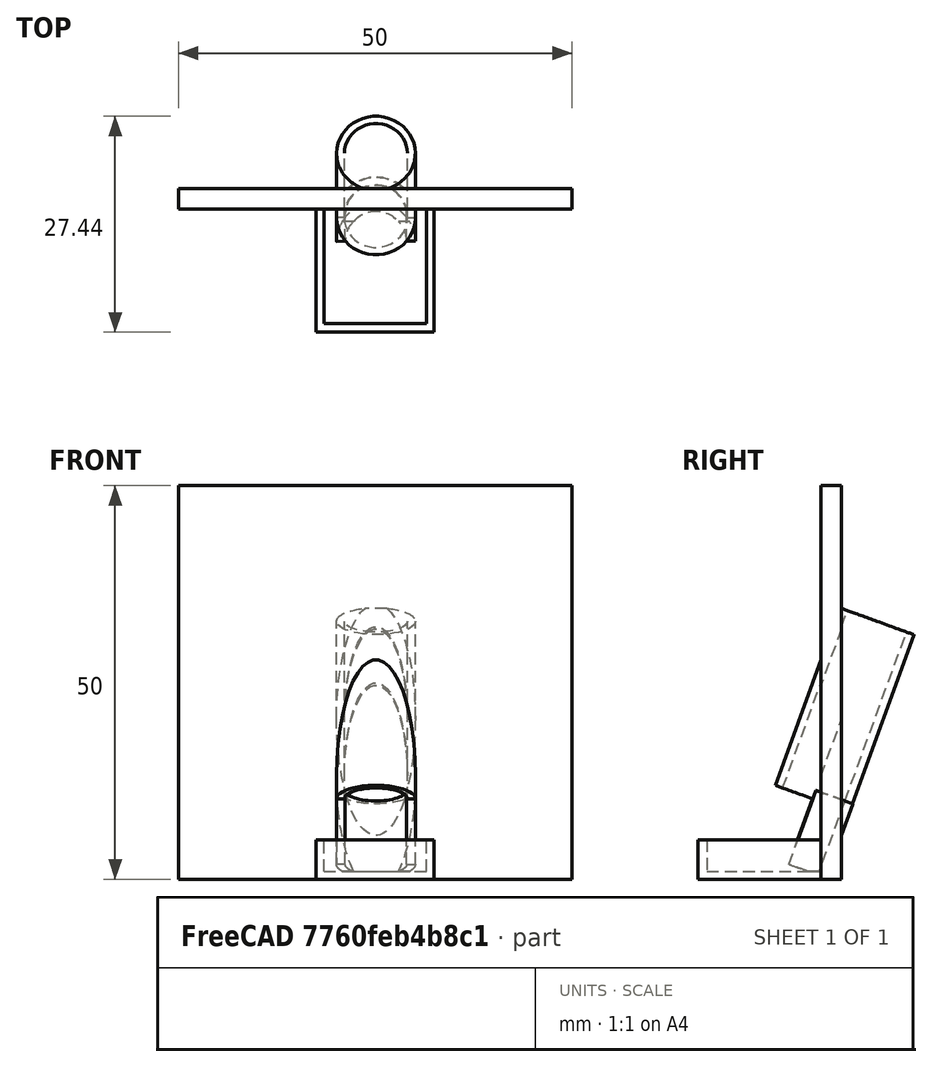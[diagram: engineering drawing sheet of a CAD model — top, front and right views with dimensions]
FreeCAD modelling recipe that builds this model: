
FCSTD DOCUMENT  (FreeCAD 0.21R33694 (Git))
Label: reward_chute_Wall_v3
License: All rights reserved
LicenseURL: https://en.wikipedia.org/wiki/All_rights_reserved
objects: Part::Box×3, Part::Cut×2, Sketcher::SketchObject×1, Part::Extrusion×1, Part::Cylinder×1, Part::FeaturePython×1, Part::MultiFuse×1
note: 10 computed .brp shape members not serialized (recipe doc carries the construction recipe); baked Part::Feature solids carry a one-line shape summary decoded from their .brp

FEATURE [Part::Box] Box  label="Cube"
  AttacherType = Attacher::AttachEngine3D
  Height = 2.6
  Length = 50
  Width = 50
FEATURE [Sketcher::SketchObject] Sketch
  FullyConstrained = false
  sketch-geometry (4):
    g0: ArcOfCircle CenterX=25.1024 CenterY=25.146 CenterZ=0 NormalX=0 NormalY=0 NormalZ=1 AngleXU=0 Radius=3.90266 StartAngle=0 EndAngle=3.14159
    g1: ArcOfCircle CenterX=25.1024 CenterY=25.146 CenterZ=0 NormalX=0 NormalY=0 NormalZ=1 AngleXU=0 Radius=5.0073 StartAngle=0 EndAngle=3.1459
    g2: LineSegment StartX=29.005 StartY=25.146 StartZ=0 EndX=30.1097 EndY=25.146 EndZ=0
    g3: LineSegment StartX=21.1997 StartY=25.146 StartZ=0 EndX=20.0951 EndY=25.1244 EndZ=0
  constraints (6):
    c: Coincident(g1,g0)
    c: Coincident(g2,g0)
    c: Coincident(g2,g1)
    c: Horizontal(g2)
    c: Coincident(g3,g0)
    c: Coincident(g3,g1)
FEATURE [Part::Extrusion] Extrude
  Base = -> Sketch
  Dir = (0,0,1)
  DirMode = 2
  FaceMakerClass = Part::FaceMakerBullseye
  LengthFwd = 10
  LengthRev = 0
  Placement = pos=(0,39.5,-27.7) rot=(1,0,0;1.22173rad)
  Solid = true
  Symmetric = false
FEATURE [Part::Cylinder] Cylinder
  Angle = 360
  AttacherType = Attacher::AttachEngine3D
  FirstAngle = 0
  Height = 35
  Placement = pos=(25.1,48,-4) rot=(1,0,0;1.22173rad)
  Radius = 4
  SecondAngle = 0
FEATURE [Part::FeaturePython] Tube  # WARN: FeaturePython — macro-defined, semantics opaque (R4)
  AttacherType = Attacher::AttachEngine3D
  Height = 24
  InnerRadius = 4
  OuterRadius = 5
  Placement = pos=(25.1,39.77,-1.1) rot=(1,0,0;1.22173rad)
FEATURE [Part::Box] Box001  label="Cube001"
  AttacherType = Attacher::AttachEngine3D
  Height = 18
  Length = 15
  Placement = pos=(17.5,45,-7.13) rot=(0,0,1;0rad)
  Width = 5
FEATURE [Part::Box] Box002  label="Cube002"
  AttacherType = Attacher::AttachEngine3D
  Height = 16
  Length = 13
  Placement = pos=(18.5,45,-6) rot=(0,0,1;0rad)
  Width = 4
FEATURE [Part::Cut] Cut001
  Base = -> Box001
  Placement = pos=(0,0,-8.5) rot=(0,0,1;0rad)
  Tool = -> Box002
FEATURE [Part::Cut] Cut
  Base = -> Box
  Tool = -> Cylinder
FEATURE [Part::MultiFuse] Fusion
  Placement = pos=(0,0,0) rot=(-1,0,0;1.5708rad)
  Shapes = -> [Extrude,Tube,Cut001,Cut]
